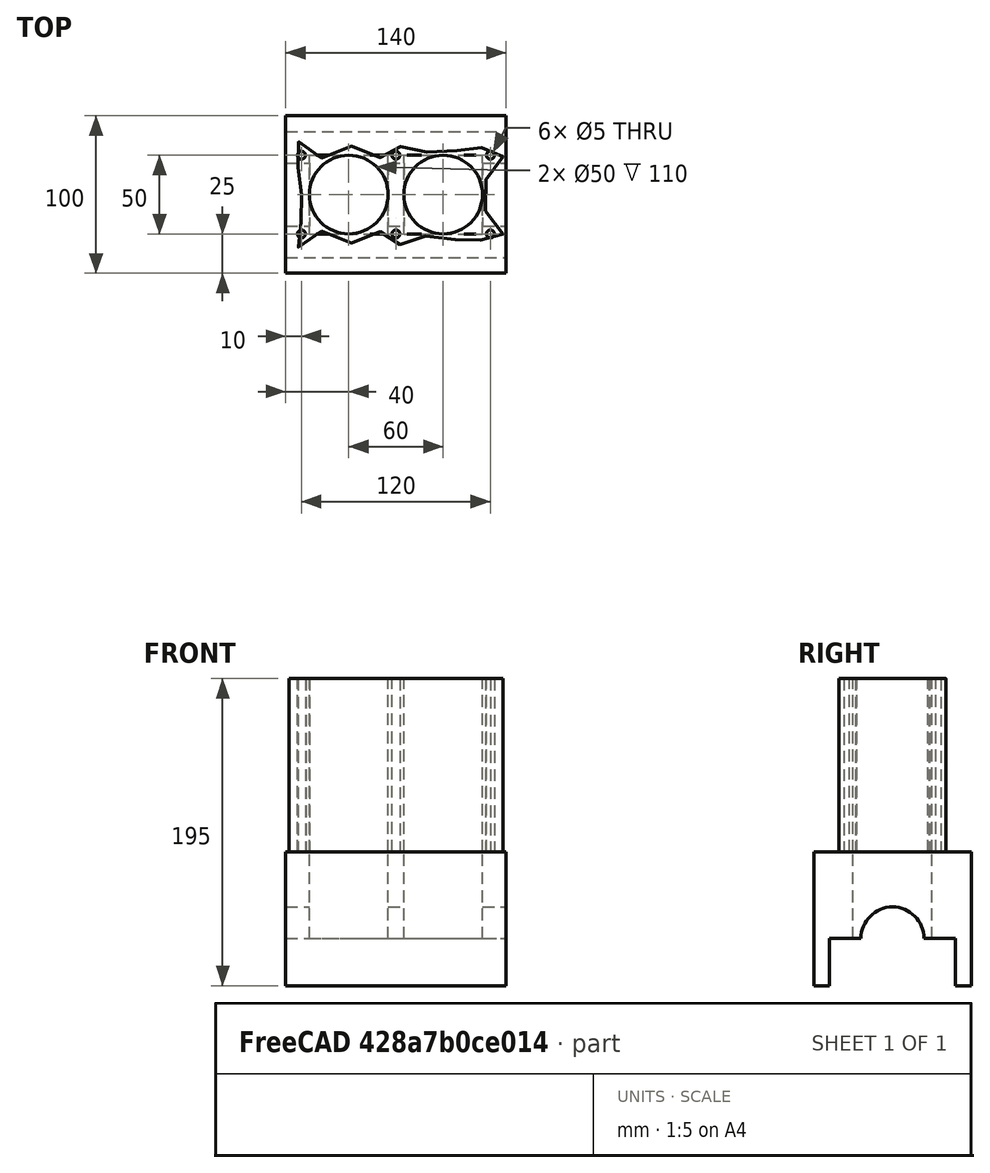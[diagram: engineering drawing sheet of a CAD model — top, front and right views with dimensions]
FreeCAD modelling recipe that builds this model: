
FCSTD DOCUMENT  (FreeCAD 0.18R16146 (Git))
Label: meshfile.inp
License: CC-BY 3.0
LicenseURL: http://creativecommons.org/licenses/by/3.0/
objects: Part::Part2DObjectPython×8, Part::Extrusion×7, Part::Box×5, Part::Cut×5, Part::Cylinder×3, Part::MultiFuse×3, Part::Mirroring×3, Fem::FemMeshShapeNetgenObject×2, Part::Feature×2, App::DocumentObjectGroup×1, Part::MultiCommon×1
note: 37 computed .brp shape members not serialized (recipe doc carries the construction recipe); baked Part::Feature solids carry a one-line shape summary decoded from their .brp

FEATURE [Part::Box] Box  label="Billet"
  AttacherType = Attacher::AttachEngine3D
  Height = 110
  Length = 140
  Placement = pos=(0,-40,0) rot=(0,0,1;0rad)
  Width = 80
FEATURE [Part::Cylinder] Cylinder  label="Cylinder 1"
  Angle = 360
  AttacherType = Attacher::AttachEngine3D
  Height = 110
  Placement = pos=(40,0,0) rot=(0,0,1;0rad)
  Radius = 25
FEATURE [Part::Cylinder] Cylinder001  label="Cylinder 2"
  Angle = 360
  AttacherType = Attacher::AttachEngine3D
  Height = 110
  Placement = pos=(100,0,0) rot=(0,0,1;0rad)
  Radius = 25
FEATURE [Part::MultiFuse] Fusion  label="Cylinders"
  Shapes = -> [Cylinder,Cylinder001]
FEATURE [Part::Cut] Cut  label="Bored Block"
  Base = -> Box
  Tool = -> Fusion
FEATURE [Part::Box] Box001  label="Crankcase Billet"
  AttacherType = Attacher::AttachEngine3D
  Height = 85
  Length = 140
  Placement = pos=(0,-50,-85) rot=(0,0,1;0rad)
  Width = 100
FEATURE [Part::Box] Box002  label="Bearing carve"
  AttacherType = Attacher::AttachEngine3D
  Height = 30
  Length = 140
  Placement = pos=(0,-40,-85) rot=(0,0,1;0rad)
  Width = 80
FEATURE [Part::Cut] Cut001  label="Carved crankcase"
  Base = -> Box001
  Tool = -> Box002
FEATURE [Part::Cylinder] Cylinder002  label="Cranshaft carve"
  Angle = 360
  AttacherType = Attacher::AttachEngine3D
  Height = 140
  Placement = pos=(0,0,-55) rot=(0,1,0;1.5708rad)
  Radius = 20
FEATURE [Part::Cut] Cut002  label="Crankcase with journals"
  Base = -> Cut001
  Tool = -> Cylinder002
FEATURE [Part::Box] Box003  label="Box carve 1"
  AttacherType = Attacher::AttachEngine3D
  Height = 55
  Length = 50
  Placement = pos=(15,-25,-55) rot=(0,0,1;0rad)
  Width = 50
FEATURE [Part::Box] Box004  label="Box carve 2"
  AttacherType = Attacher::AttachEngine3D
  Height = 55
  Length = 50
  Placement = pos=(75,-25,-55) rot=(0,0,1;0rad)
  Width = 50
FEATURE [Part::MultiFuse] Fusion001  label="Box carvers"
  Shapes = -> [Box003,Box004]
FEATURE [Part::Cut] Cut003  label="Crankcase"
  Base = -> Cut002
  Tool = -> Fusion001
FEATURE [Part::Part2DObjectPython] Circle003  label="Bolt 007"  # Draft 2D object (typed FeaturePython)
  FirstAngle = 0
  LastAngle = 0
  MapMode = 5
  Placement = pos=(10,25,110) rot=(0,0,1;0rad)
  Radius = 2.5
FEATURE [Part::Mirroring] Part__Mirroring  label="Bolt 4"
  Base = (0,0,0)
  Normal = (0,1,0)
  Source = -> Circle003
FEATURE [Part::Extrusion] Extrude  label="Head bolt bore 1"
  Base = -> Circle003
  Dir = (0,0,-110)
  DirMode = 0
  FaceMakerClass = Part::FaceMakerExtrusion
  LengthFwd = 0
  LengthRev = 0
  Solid = false
  Symmetric = false
FEATURE [Part::Extrusion] Extrude003  label="Head bolt bore 4"
  Base = -> Part__Mirroring
  Dir = (0,0,-110)
  DirMode = 0
  FaceMakerClass = Part::FaceMakerExtrusion
  LengthFwd = 0
  LengthRev = 0
  Solid = false
  Symmetric = false
FEATURE [Part::Part2DObjectPython] Circle004  label="Bolt 008"  # Draft 2D object (typed FeaturePython)
  FirstAngle = 0
  LastAngle = 0
  MapMode = 5
  Placement = pos=(70,25,110) rot=(0,0,1;0rad)
  Radius = 2.5
FEATURE [Part::Mirroring] Part__Mirroring001  label="Bolt 5"
  Base = (0,0,0)
  Normal = (0,1,0)
  Source = -> Circle004
FEATURE [Part::Extrusion] Extrude001  label="Head bolt bore 2"
  Base = -> Circle004
  Dir = (0,0,-110)
  DirMode = 0
  FaceMakerClass = Part::FaceMakerExtrusion
  LengthFwd = 0
  LengthRev = 0
  Solid = false
  Symmetric = false
FEATURE [Part::Extrusion] Extrude004  label="Head bolt bore 5"
  Base = -> Part__Mirroring001
  Dir = (0,0,-110)
  DirMode = 0
  FaceMakerClass = Part::FaceMakerExtrusion
  LengthFwd = 0
  LengthRev = 0
  Solid = false
  Symmetric = false
FEATURE [Part::Part2DObjectPython] Circle005  label="Bolt 009"  # Draft 2D object (typed FeaturePython)
  FirstAngle = 0
  LastAngle = 0
  MapMode = 5
  Placement = pos=(130,25,110) rot=(0,0,1;0rad)
  Radius = 2.5
FEATURE [Part::Mirroring] Part__Mirroring002  label="Bolt 6"
  Base = (0,0,0)
  Normal = (0,1,0)
  Source = -> Circle005
FEATURE [Part::Extrusion] Extrude002  label="Head bolt bore 3"
  Base = -> Circle005
  Dir = (0,0,-110)
  DirMode = 0
  FaceMakerClass = Part::FaceMakerExtrusion
  LengthFwd = 0
  LengthRev = 0
  Solid = false
  Symmetric = false
FEATURE [Part::Extrusion] Extrude005  label="Head bolt bore 6"
  Base = -> Part__Mirroring002
  Dir = (0,0,-110)
  DirMode = 0
  FaceMakerClass = Part::FaceMakerExtrusion
  LengthFwd = 0
  LengthRev = 0
  Solid = false
  Symmetric = false
FEATURE [Part::MultiFuse] Fusion002  label="Head bolt boreholes"
  Shapes = -> [Extrude,Extrude001,Extrude002,Extrude003,Extrude004,Extrude005]
FEATURE [Part::Cut] Cut004  label="Block with headbolts"
  Base = -> Cut
  Tool = -> Fusion002
FEATURE [Part::Part2DObjectPython] Polygon004  # Draft 2D object (typed FeaturePython)
  ChamferSize = 0
  DrawMode = 0
  FacesNumber = 14
  FilletRadius = 0
  MapMode = 5
  Placement = pos=(40,0,110) rot=(0,0,1;0rad)
  Radius = 30
FEATURE [Part::Part2DObjectPython] Polygon005  # Draft 2D object (typed FeaturePython)
  ChamferSize = 0
  DrawMode = 0
  FacesNumber = 14
  FilletRadius = 0
  MapMode = 5
  Placement = pos=(100,0,110) rot=(0,0,1;0rad)
  Radius = 30
FEATURE [Part::Part2DObjectPython] Polygon006  # Draft 2D object (typed FeaturePython)
  ChamferSize = 0
  DrawMode = 0
  FacesNumber = 22
  FilletRadius = 0
  MapMode = 5
  Placement = pos=(40,0,110) rot=(0,0,1;0rad)
  Radius = 45
FEATURE [Part::Part2DObjectPython] Polygon007  # Draft 2D object (typed FeaturePython)
  ChamferSize = 0
  DrawMode = 0
  FacesNumber = 22
  FilletRadius = 0
  MapMode = 5
  Placement = pos=(100,0,110) rot=(0,0,1;0rad)
  Radius = 45
FEATURE [App::DocumentObjectGroup] Construction
  Group = -> [Polygon004,Polygon005,Polygon006,Polygon007]
FEATURE [Part::Part2DObjectPython] BSpline001  # Draft 2D object (typed FeaturePython)
  Closed = true
  MapMode = 5
  Points = (36) [(1.74614e-119,4133350,123145000000000),(625142000,802825,123145000000000),(463715000,11434000000,123145000000000),+33 more]
FEATURE [Part::Extrusion] Extrude006  label="Extruded spline"
  Base = -> BSpline001
  Dir = (0,0,-110)
  DirMode = 0
  FaceMakerClass = Part::FaceMakerExtrusion
  LengthFwd = 0
  LengthRev = 0
  Solid = false
  Symmetric = false
FEATURE [Part::MultiCommon] Common  label="Engine block"
  Shapes = -> [Extrude006,Cut004]
FEATURE [Fem::FemMeshShapeNetgenObject] FEMMeshNetgen
  Fineness = 2
  GrowthRate = 0.3
  MaxSize = 1000
  NbSegsPerEdge = 1
  NbSegsPerRadius = 2
  Optimize = true
  SecondOrder = false
  Shape = -> Cut003
FEATURE [Part::Feature] Face
  shape: bbox 138.4 x 70.75 x 2e-07 mm, 1 faces, 0 solids (baked)
FEATURE [Part::Feature] Face001
  shape: bbox 138.4 x 70.75 x 2e-07 mm, 1 faces, 0 solids (baked)
FEATURE [Fem::FemMeshShapeNetgenObject] FEMMeshNetgen001
  Fineness = 2
  GrowthRate = 0.3
  MaxSize = 3
  NbSegsPerEdge = 1
  NbSegsPerRadius = 2
  Optimize = true
  SecondOrder = false
  Shape = -> Face001
